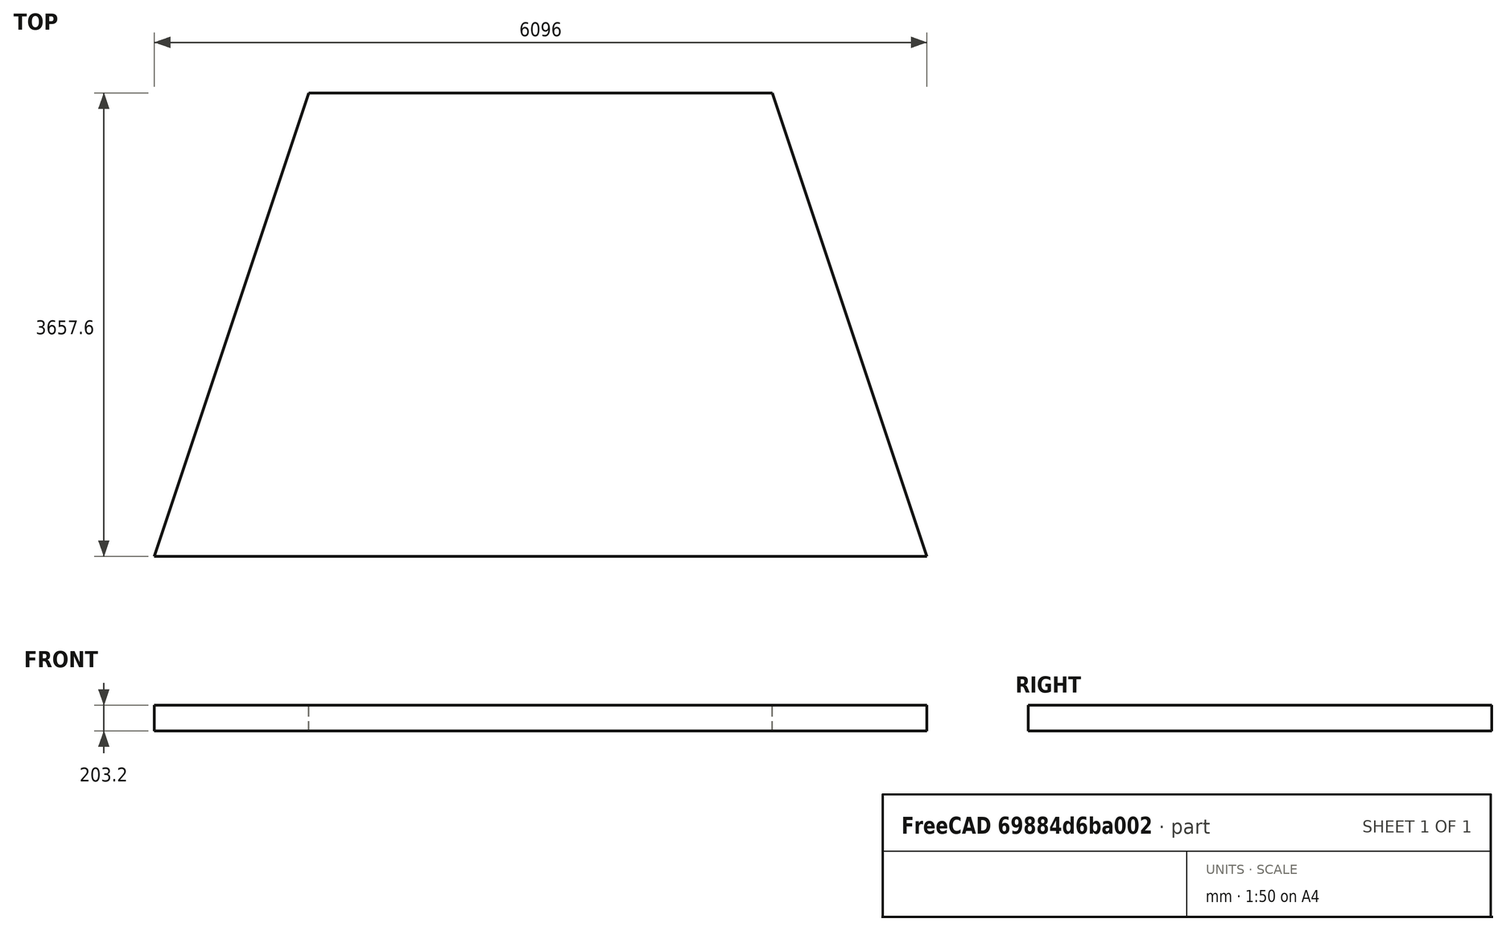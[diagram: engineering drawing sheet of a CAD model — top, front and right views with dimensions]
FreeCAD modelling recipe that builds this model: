
FCSTD DOCUMENT  (FreeCAD 0.20R29177 (Git))
Label: Roof
License: All rights reserved
LicenseURL: http://en.wikipedia.org/wiki/All_rights_reserved
objects: Sketcher::SketchObject×1, PartDesign::Pad×1, PartDesign::Body×1
note: 4 computed .brp shape members not serialized (recipe doc carries the construction recipe); baked Part::Feature solids carry a one-line shape summary decoded from their .brp

FEATURE [Sketcher::SketchObject] Sketch
  FullyConstrained = true
  MapMode = 5
  Support = -> [XY_Plane]
  sketch-geometry (6):
    g0: LineSegment StartX=-3048 StartY=-1828.8 StartZ=0 EndX=3048 EndY=-1828.8 EndZ=0
    g1: LineSegment StartX=3048 StartY=-1828.8 StartZ=0 EndX=1828.8 EndY=1828.8 EndZ=0
    g2: LineSegment StartX=1828.8 StartY=1828.8 StartZ=0 EndX=-1828.8 EndY=1828.8 EndZ=0
    g3: LineSegment StartX=-1828.8 StartY=1828.8 StartZ=0 EndX=-3048 EndY=-1828.8 EndZ=0
    g4: GeomPoint X=0 Y=-1828.8 Z=0
    g5: GeomPoint X=0 Y=1828.8 Z=0
  constraints (14):
    c: Horizontal(g0)
    c: Coincident(g0,g1)
    c: Coincident(g1,g2)
    c: Horizontal(g2)
    c: Coincident(g2,g3)
    c: Coincident(g3,g0)
    c: DistanceX(g2,g2) = 3657.6
    c: DistanceX(g0,g0) = 6096
    c: DistanceY(g-1,g2) = 1828.8
    c: DistanceY(g0,g-1) = 1828.8
    c: PointOnObject(g4,g-2)
    c: Symmetric(g0,g0,g4)
    c: PointOnObject(g5,g-2)
    c: Symmetric(g2,g1,g5)
FEATURE [PartDesign::Pad] Pad
  Direction = (0,0,1)
  Length = 203.2
  Length2 = 9.525
  Profile = -> Sketch
  ReferenceAxis = -> Sketch [N_Axis]
  Type = 0
FEATURE [PartDesign::Body] Body
  Group = -> [Sketch,Pad]
  Origin = -> Origin
  Tip = -> Pad
